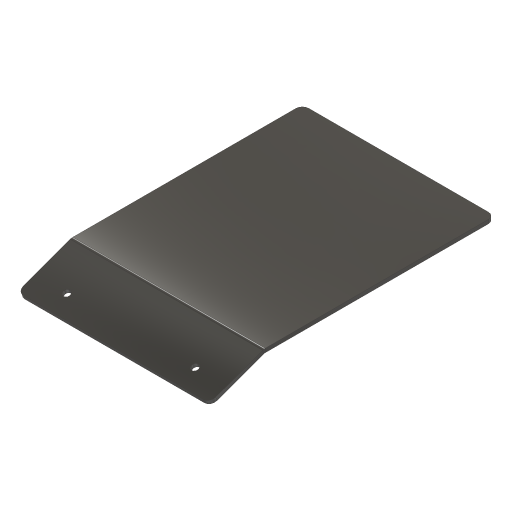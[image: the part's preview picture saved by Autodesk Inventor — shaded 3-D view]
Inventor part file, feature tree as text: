
AUTODESK INVENTOR PART (.ipt)
format: ipt  version: 2024.3 (Build 283343000, 343)  size: 268,288 bytes
history: native  units: mm
features: sheet_metal_op x4, other x4, sketch x4, fillet x1, hole x1
ambient origin geometry x8: Origin, YZ Plane, XZ Plane, XY Plane, X Axis, Y Axis, Z Axis, Center Point
bodies: Body1 (feature_tree)
feature tree (14):
  sheet_metal_op  "Face2"
  sheet_metal_op  "Flange2"
  fillet  "Fillet1"  Radius=150.0mm
  other  "Decal2"
  hole  "Hole1"  [1 undecoded]
  sketch  "Sketch3"  dims[d12=180.0mm d13=3.0mm]
  other  "Plate3"
  sketch  "Sketch4"  dims[d14=3.0mm]
  other  "Plate4"
  sheet_metal_op  "Bend2"
  sheet_metal_op  "Corner2"
  sketch  "Sketch6"  dims[d15=1.5mm]
  other  "Image2"
  sketch  "Sketch7"  dims[d16=6.0mm d17=3.0mm d18=45.0mm d19=3.490659mm d20=3.0mm d21=12.0mm d22=3.0mm d23=3.0mm d24=5.0mm d50=178.942038mm d51=140.0mm d52=135.0mm d53=3.0mm d62=100.0mm d63=150.0mm d64=25.0mm d65=14.5mm d66=5.5mm d67=6.0mm d68=10.4mm d69=2.0mm d70=90.0deg d71=3.0mm d72=20.594885mm]
note: 1 required parameter value undecoded (feature->parameter linkage not recoverable at this tier; creation-order binding heuristic only, values carry confidence <= 0.55)
